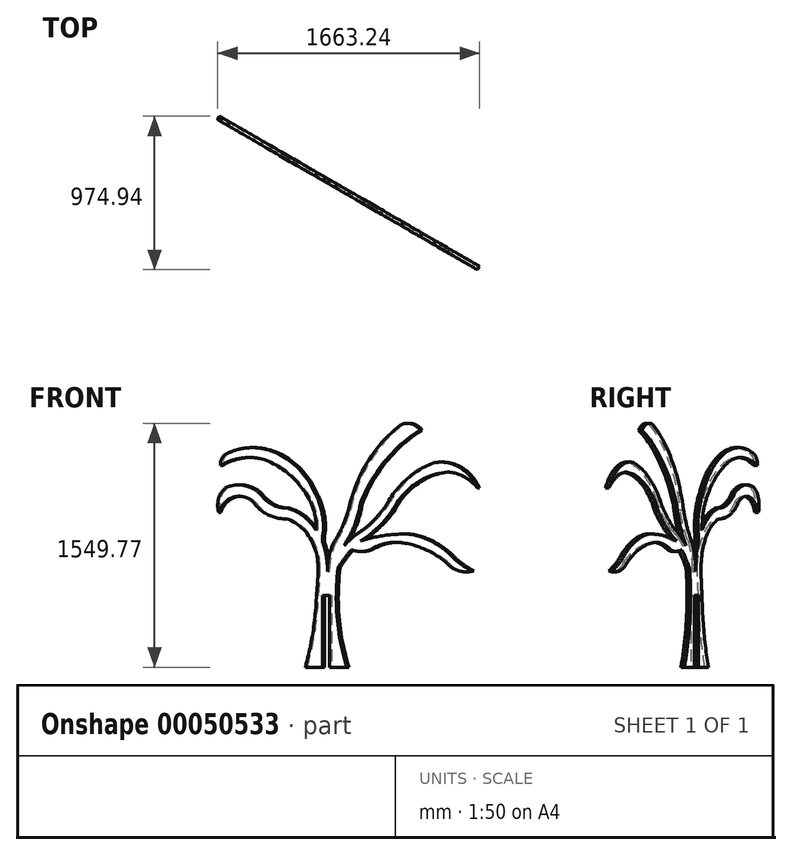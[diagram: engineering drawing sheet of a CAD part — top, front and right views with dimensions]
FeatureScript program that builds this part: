
annotation { "Feature Type Name" : "Feature", "Feature Type Description" : "" }
export const myFeature = defineFeature(function(context is Context, id is Id, definition is map)
    precondition{}
    {
        {
            var Q0;
            Q0=qCreatedBy(makeId("Front.planeOp"),FACE);
            var sketch = newSketch(context, id + "F0", { "sketchPlane" : qUnion([Q0])});
            skLineSegment(sketch, "E0", {"start": v(-55.31, -3.23) * mm, "end": v(-55.31, -3.23) * mm});
            skArc(sketch, "E1", {"start": v(155.05, 231.17) * mm, "mid": v(109.4, 198.17) * mm, "end": v(66.96, 161.12) * mm});
            skArc(sketch, "E2", {"start": v(155.05, 231.17) * mm, "mid": v(179.89, 245.26) * mm, "end": v(204.15, 260.3) * mm});
            skArc(sketch, "E3", {"start": v(186.97, 187.97) * mm, "mid": v(311.11, 271.47) * mm, "end": v(418.62, 375.52) * mm});
            skArc(sketch, "E4.trimOffspring", {"start": v(121.99, 133.28) * mm, "mid": v(70.09, 78.5) * mm, "end": v(24.27, 18.55) * mm});
            skArc(sketch, "E5", {"start": v(371.22, 409.24) * mm, "mid": v(383.26, 425.82) * mm, "end": v(393.71, 443.43) * mm});
            skArc(sketch, "E6", {"start": v(418.62, 375.52) * mm, "mid": v(419.74, 377.37) * mm, "end": v(420.82, 379.24) * mm});
            skArc(sketch, "E7", {"start": v(-123.4, 23.95) * mm, "mid": v(-187.26, 215.38) * mm, "end": v(-353.24, 330.14) * mm});
            skArc(sketch, "E8", {"start": v(-353.24, 330.14) * mm, "mid": v(-343.71, 326.68) * mm, "end": v(-333.97, 323.87) * mm});
            skArc(sketch, "E9", {"start": v(-348.86, 398.8) * mm, "mid": v(-328.05, 391.52) * mm, "end": v(-306.82, 385.57) * mm});
            skArc(sketch, "E10", {"start": v(-55.31, -3.23) * mm, "mid": v(-62.2, 92.76) * mm, "end": v(-92.03, 184.25) * mm});
            skArc(sketch, "E11", {"start": v(-133.98, -149.73) * mm, "mid": v(-126.05, -63.05) * mm, "end": v(-123.4, 23.95) * mm});
            skArc(sketch, "E12", {"start": v(24.27, 18.55) * mm, "mid": v(16.93, -301.16) * mm, "end": v(88.54, -612.83) * mm});
            skPoint(sketch, "E13.start.orphan", {"position": v(0, -612.83) * mm});
            skLineSegment(sketch, "E14", {"start": v(88.54, -612.83) * mm, "end": v(-38.46, -612.83) * mm});
            skLineSegment(sketch, "E15", {"start": v(-63.86, -155.63) * mm, "end": v(-38.46, -155.63) * mm});
            skLineSegment(sketch, "E16", {"start": v(-38.46, -155.63) * mm, "end": v(-38.46, -612.83) * mm});
            skLineSegment(sketch, "E17", {"start": v(-63.86, -155.63) * mm, "end": v(-89.26, -155.63) * mm});
            skLineSegment(sketch, "E18", {"start": v(-89.26, -155.63) * mm, "end": v(-89.26, -612.83) * mm});
            skPoint(sketch, "E19.start.orphan", {"position": v(-63.86, -612.83) * mm});
            skLineSegment(sketch, "E20.trimOffspring", {"start": v(-89.26, -612.83) * mm, "end": v(-216.26, -612.83) * mm});
            skArc(sketch, "E21", {"start": v(-216.26, -612.83) * mm, "mid": v(-159.76, -384) * mm, "end": v(-133.98, -149.73) * mm});
            skPoint(sketch, "E22.orphan", {"position": v(-216.26, -483.1) * mm});
            skLineSegment(sketch, "E23", {"start": v(-55.31, -3.23) * mm, "end": v(-55.31, 36.53) * mm});
            skArc(sketch, "E24", {"start": v(565.58, 231.17) * mm, "mid": v(374.43, 225.73) * mm, "end": v(186.97, 187.97) * mm});
            skArc(sketch, "E25", {"start": v(502, 176.52) * mm, "mid": v(385.8, 175.81) * mm, "end": v(275.14, 140.4) * mm});
            skArc(sketch, "E26", {"start": v(121.99, 133.28) * mm, "mid": v(199.22, 122.74) * mm, "end": v(275.14, 140.4) * mm});
            skPoint(sketch, "E27.end.orphan", {"position": v(-297.08, 479.96) * mm});
            skArc(sketch, "E28", {"start": v(-212.24, 332.74) * mm, "mid": v(-257.17, 363.38) * mm, "end": v(-306.82, 385.57) * mm});
            skPoint(sketch, "E29.endSnap0", {"position": v(-372.54, 684.1) * mm});
            skArc(sketch, "E30.trimOffspring", {"start": v(-137.88, 259.33) * mm, "mid": v(-172.63, 298.5) * mm, "end": v(-212.24, 332.74) * mm});
            skArc(sketch, "E31", {"start": v(137.84, 692.04) * mm, "mid": v(134.66, 697.54) * mm, "end": v(131.42, 703) * mm});
            skArc(sketch, "E32", {"start": v(144.26, 702.13) * mm, "mid": v(137.85, 702.7) * mm, "end": v(131.42, 703) * mm});
            skArc(sketch, "E33.trimOffspring", {"start": v(260.66, 300.83) * mm, "mid": v(318.81, 352.1) * mm, "end": v(371.22, 409.24) * mm});
            skArc(sketch, "E34", {"start": v(137.84, 692.04) * mm, "mid": v(141.06, 697.08) * mm, "end": v(144.26, 702.13) * mm});
            skPoint(sketch, "E35.center.orphan", {"position": v(216.37, 756.13) * mm});
            skArc(sketch, "E36", {"start": v(204.15, 260.3) * mm, "mid": v(233.66, 278.82) * mm, "end": v(260.66, 300.83) * mm});
            skPoint(sketch, "E37.end.orphan", {"position": v(216.37, 824.78) * mm});
            skPoint(sketch, "E38.end.orphan", {"position": v(248.93, 730.67) * mm});
            skPoint(sketch, "E38.start.orphan", {"position": v(345.62, 730.67) * mm});
            skArc(sketch, "E39", {"start": v(66.96, 161.12) * mm, "mid": v(143.76, 287.68) * mm, "end": v(187.87, 429) * mm});
            skArc(sketch, "E40", {"start": v(0, 191.46) * mm, "mid": v(57.57, 284.2) * mm, "end": v(98.77, 385.27) * mm});
            skArc(sketch, "E41", {"start": v(0, 191.46) * mm, "mid": v(-41.22, 97.97) * mm, "end": v(-55.31, -3.23) * mm});
            skPoint(sketch, "E42.trimOffspring.start.orphan", {"position": v(0, 85.53) * mm});
            skArc(sketch, "E43", {"start": v(98.77, 385.27) * mm, "mid": v(94.77, 374.06) * mm, "end": v(91.26, 362.68) * mm});
            skArc(sketch, "E44", {"start": v(236.83, 535.32) * mm, "mid": v(200.32, 466.27) * mm, "end": v(179.64, 390.96) * mm});
            skPoint(sketch, "E45.start.orphan", {"position": v(-281.4, 684.1) * mm});
            skArc(sketch, "E46", {"start": v(-137.88, 259.33) * mm, "mid": v(-148.6, 365.33) * mm, "end": v(-194.45, 461.5) * mm});
            skArc(sketch, "E47", {"start": v(-218.2, 495.85) * mm, "mid": v(-207.55, 477.83) * mm, "end": v(-194.45, 461.5) * mm});
            skArc(sketch, "E48", {"start": v(-83.71, 253.63) * mm, "mid": v(-95.99, 378) * mm, "end": v(-145.88, 492.58) * mm});
            skArc(sketch, "E49", {"start": v(-83.71, 253.63) * mm, "mid": v(-89.87, 219.18) * mm, "end": v(-92.03, 184.25) * mm});
            skArc(sketch, "E50", {"start": v(819.75, 50.46) * mm, "mid": v(668.75, 133.36) * mm, "end": v(502, 176.52) * mm});
            skArc(sketch, "E51", {"start": v(852.07, 98) * mm, "mid": v(717.17, 182.53) * mm, "end": v(565.58, 231.17) * mm});
            skArc(sketch, "E52", {"start": v(819.75, 50.46) * mm, "mid": v(906.04, -0.15) * mm, "end": v(1006.08, 0) * mm});
            skArc(sketch, "E53", {"start": v(852.07, 98) * mm, "mid": v(924.57, 41.92) * mm, "end": v(1006.08, 0) * mm});
            skArc(sketch, "E54", {"start": v(724.16, 685.31) * mm, "mid": v(522.79, 579.11) * mm, "end": v(371.22, 409.24) * mm});
            skArc(sketch, "E55", {"start": v(826.36, 627.26) * mm, "mid": v(591.13, 552.19) * mm, "end": v(418.62, 375.52) * mm});
            skArc(sketch, "E56", {"start": v(1046.62, 525.1) * mm, "mid": v(946.36, 597.45) * mm, "end": v(826.36, 627.26) * mm});
            skPoint(sketch, "E57.trimOffspring.end.orphan", {"position": v(418.62, 525.06) * mm});
            skArc(sketch, "E58", {"start": v(1046.62, 525.1) * mm, "mid": v(911.76, 658.27) * mm, "end": v(724.16, 685.31) * mm});
            skArc(sketch, "E59", {"start": v(485.86, 927.78) * mm, "mid": v(241.24, 692.97) * mm, "end": v(98.77, 385.27) * mm});
            skArc(sketch, "E60", {"start": v(625.5, 891.74) * mm, "mid": v(368.03, 696.93) * mm, "end": v(187.87, 429) * mm});
            skArc(sketch, "E61", {"start": v(625.5, 891.74) * mm, "mid": v(561.7, 933.14) * mm, "end": v(485.86, 927.78) * mm});
            skArc(sketch, "E62", {"start": v(-194.45, 461.5) * mm, "mid": v(-342.8, 618.7) * mm, "end": v(-538.44, 710.59) * mm});
            skArc(sketch, "E63", {"start": v(-145.88, 492.58) * mm, "mid": v(-304.25, 679.85) * mm, "end": v(-529.91, 775.92) * mm});
            skArc(sketch, "E64", {"start": v(-538.44, 710.59) * mm, "mid": v(-692.61, 714.84) * mm, "end": v(-839.55, 667.98) * mm});
            skArc(sketch, "E65", {"start": v(-782.74, 747.52) * mm, "mid": v(-825.6, 718.07) * mm, "end": v(-839.55, 667.98) * mm});
            skArc(sketch, "E66", {"start": v(-529.91, 775.92) * mm, "mid": v(-658.27, 779.03) * mm, "end": v(-782.74, 747.52) * mm});
            skArc(sketch, "E67", {"start": v(-600.93, 437.88) * mm, "mid": v(-489.61, 355.21) * mm, "end": v(-353.24, 330.14) * mm});
            skArc(sketch, "E68", {"start": v(-600.93, 437.88) * mm, "mid": v(-743.44, 468.04) * mm, "end": v(-850.91, 369.7) * mm});
            skArc(sketch, "E69", {"start": v(-544.12, 486.17) * mm, "mid": v(-455.8, 419.53) * mm, "end": v(-347.12, 398.86) * mm});
            skArc(sketch, "E70", {"start": v(-544.12, 486.17) * mm, "mid": v(-664.73, 541.87) * mm, "end": v(-796.94, 528.78) * mm});
            skArc(sketch, "E71", {"start": v(-796.94, 528.78) * mm, "mid": v(-852.2, 458.84) * mm, "end": v(-850.91, 369.7) * mm});
            skSolve(sketch);
        }
        {
            var Q0;
            Q0=makeQuery(id+"F0.imprint","IMPRINT",FACE,{"disambiguationData":[TD([[makeQuery(id+"F0.imprint","IMPRINT",EDGE,{"derivedFrom":sQuery(id+"F0.wireOp",EDGE,"E1")}),1.0]])]});
            extrude(context, id + "F1", {"entities" : qUnion([Q0]), "depth" : 25.4 * mm});
        }
        {
            var Q0;
            Q0=makeQuery(id+"F1.opExtrude","SWEPT_BODY",BODY,{"disambiguationData":[OSD([sQuery(id+"F0.wireOp",EDGE,"E1"),sQuery(id+"F0.wireOp",EDGE,"E2"),sQuery(id+"F0.wireOp",EDGE,"E3"),sQuery(id+"F0.wireOp",EDGE,"E4.trimOffspring"),sQuery(id+"F0.wireOp",EDGE,"E5"),sQuery(id+"F0.wireOp",EDGE,"E6"),sQuery(id+"F0.wireOp",EDGE,"E7"),sQuery(id+"F0.wireOp",EDGE,"E8"),sQuery(id+"F0.wireOp",EDGE,"E9"),sQuery(id+"F0.wireOp",EDGE,"E10"),sQuery(id+"F0.wireOp",EDGE,"E11"),sQuery(id+"F0.wireOp",EDGE,"E12"),sQuery(id+"F0.wireOp",EDGE,"E14"),sQuery(id+"F0.wireOp",EDGE,"E15"),sQuery(id+"F0.wireOp",EDGE,"E16"),sQuery(id+"F0.wireOp",EDGE,"E17"),sQuery(id+"F0.wireOp",EDGE,"E18"),sQuery(id+"F0.wireOp",EDGE,"E20.trimOffspring"),sQuery(id+"F0.wireOp",EDGE,"E21")])]});
            var Q1;
            Q1=makeQuery(id+"F1.opExtrude","CAP_EDGE",EDGE,{"disambiguationData":[OSD([sQuery(id+"F0.wireOp",EDGE,"E16")])],"isStart":false});
            transform(context, id + "F2", {"entities" : qUnion([Q0]), "transformType" : TransformType.ROTATION, "transformAxis" : qUnion([Q1]), "angle" : 30 * degree, "makeCopy" : false});
        }
    });
